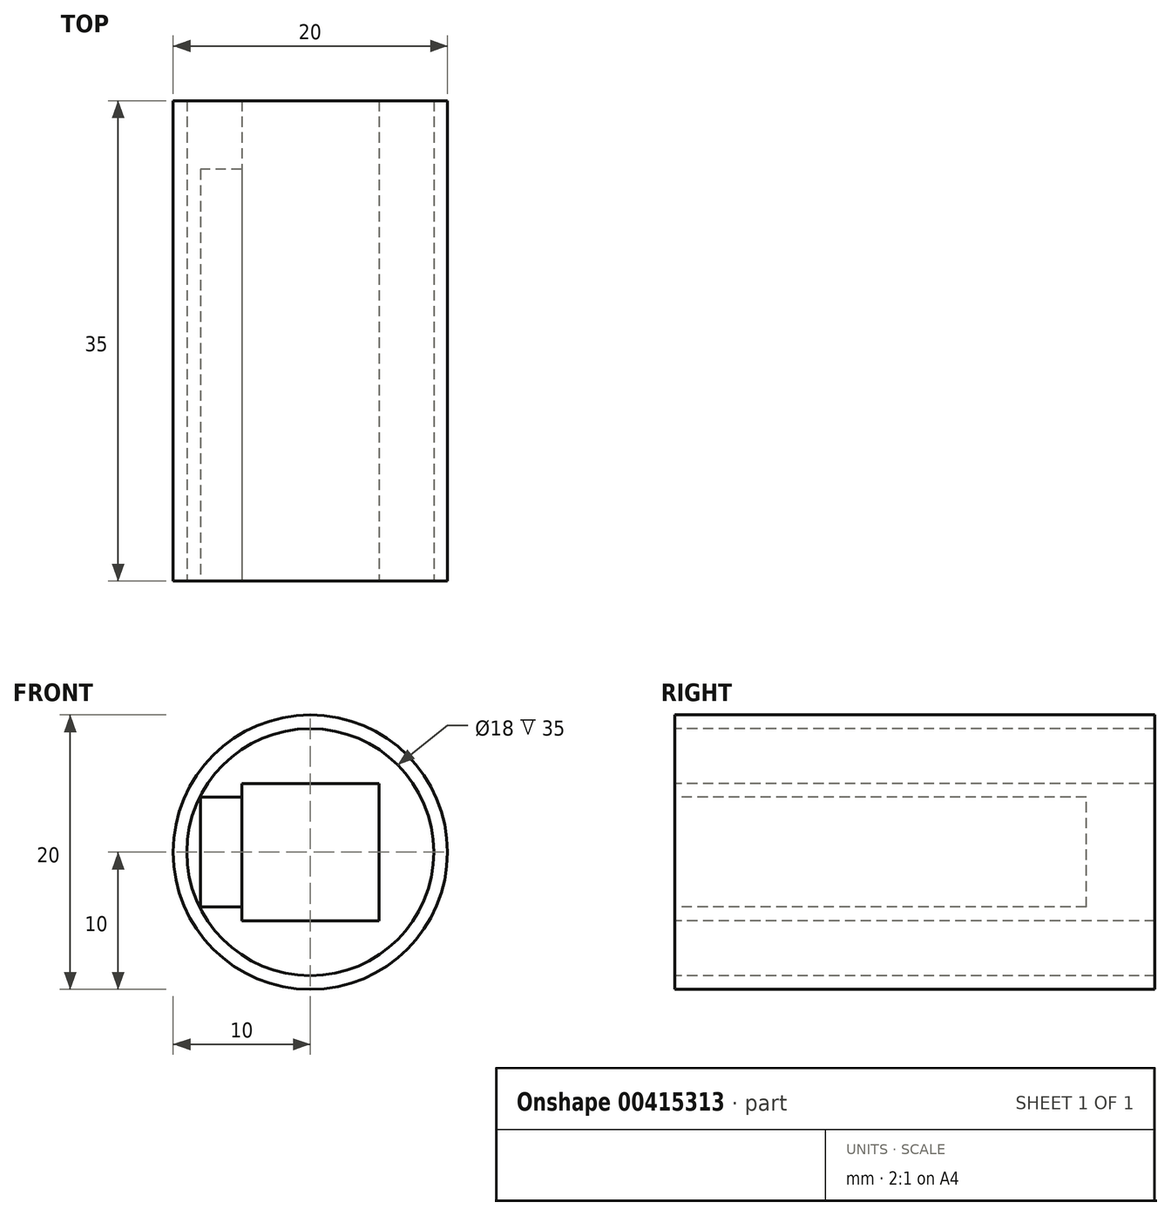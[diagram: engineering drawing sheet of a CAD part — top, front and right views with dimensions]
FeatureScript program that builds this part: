
annotation { "Feature Type Name" : "Feature", "Feature Type Description" : "" }
export const myFeature = defineFeature(function(context is Context, id is Id, definition is map)
    precondition{}
    {
        {
            var Q0;
            Q0=qCreatedBy(makeId("Front.planeOp"),FACE);
            var sketch = newSketch(context, id + "F0", { "sketchPlane" : qUnion([Q0])});
            skLineSegment(sketch, "E0.bottom", {"start": v(5, -5) * mm, "end": v(-5, -5) * mm});
            skLineSegment(sketch, "E0.top", {"start": v(5, 5) * mm, "end": v(-5, 5) * mm});
            skLineSegment(sketch, "E0.left", {"start": v(5, -5) * mm, "end": v(5, 5) * mm});
            skLineSegment(sketch, "E0.right", {"start": v(-5, -5) * mm, "end": v(-5, 5) * mm});
            skPoint(sketch, "E0.middle", {"position": v(0, 0) * mm});
            skCircle(sketch, "E1", {"center": v(0, 0) * mm, "radius": 9 * mm});
            skLineSegment(sketch, "E2.bottom", {"start": v(-5, -4) * mm, "end": v(-8, -4) * mm});
            skLineSegment(sketch, "E2.top", {"start": v(-5, 4) * mm, "end": v(-8, 4) * mm});
            skLineSegment(sketch, "E2.left", {"start": v(-5, -4) * mm, "end": v(-5, 4) * mm});
            skLineSegment(sketch, "E2.right", {"start": v(-8, -4) * mm, "end": v(-8, 4) * mm});
            skPoint(sketch, "E2.middle", {"position": v(-6.5, 0) * mm});
            skCircle(sketch, "E3", {"center": v(0, 0) * mm, "radius": 10 * mm});
            skSolve(sketch);
        }
        {
            var Q0;
            {var subQ1=sQuery(id+"F0.wireOp",EDGE,"E0.bottom");Q0=makeQuery(id+"F0.imprint","IMPRINT",FACE,{"disambiguationData":[TD([[makeQuery(id+"F0.imprint","IMPRINT",EDGE,{"derivedFrom":subQ1}),-1.0]])]});}
            extrude(context, id + "F1", {"entities" : qUnion([Q0]), "oppositeDirection" : true, "depth" : 35 * mm});
        }
        {
            var Q0;
            Q0=makeQuery(id+"F0.imprint","IMPRINT",FACE,{"disambiguationData":[TD([[makeQuery(id+"F0.imprint","IMPRINT",EDGE,{"derivedFrom":sQuery(id+"F0.wireOp",EDGE,"E1")}),-1.0]])]});
            extrude(context, id + "F2", {"entities" : qUnion([Q0]), "oppositeDirection" : true, "depth" : 35 * mm});
        }
        {
            var Q0;
            Q0=makeQuery(id+"F0.imprint","IMPRINT",FACE,{"disambiguationData":[TD([[makeQuery(id+"F0.imprint","IMPRINT",EDGE,{"derivedFrom":sQuery(id+"F0.wireOp",EDGE,"E2.bottom")}),-1.0]])]});
            extrude(context, id + "F3", {"entities" : qUnion([Q0]), "oppositeDirection" : true, "depth" : 30 * mm});
        }
    });
